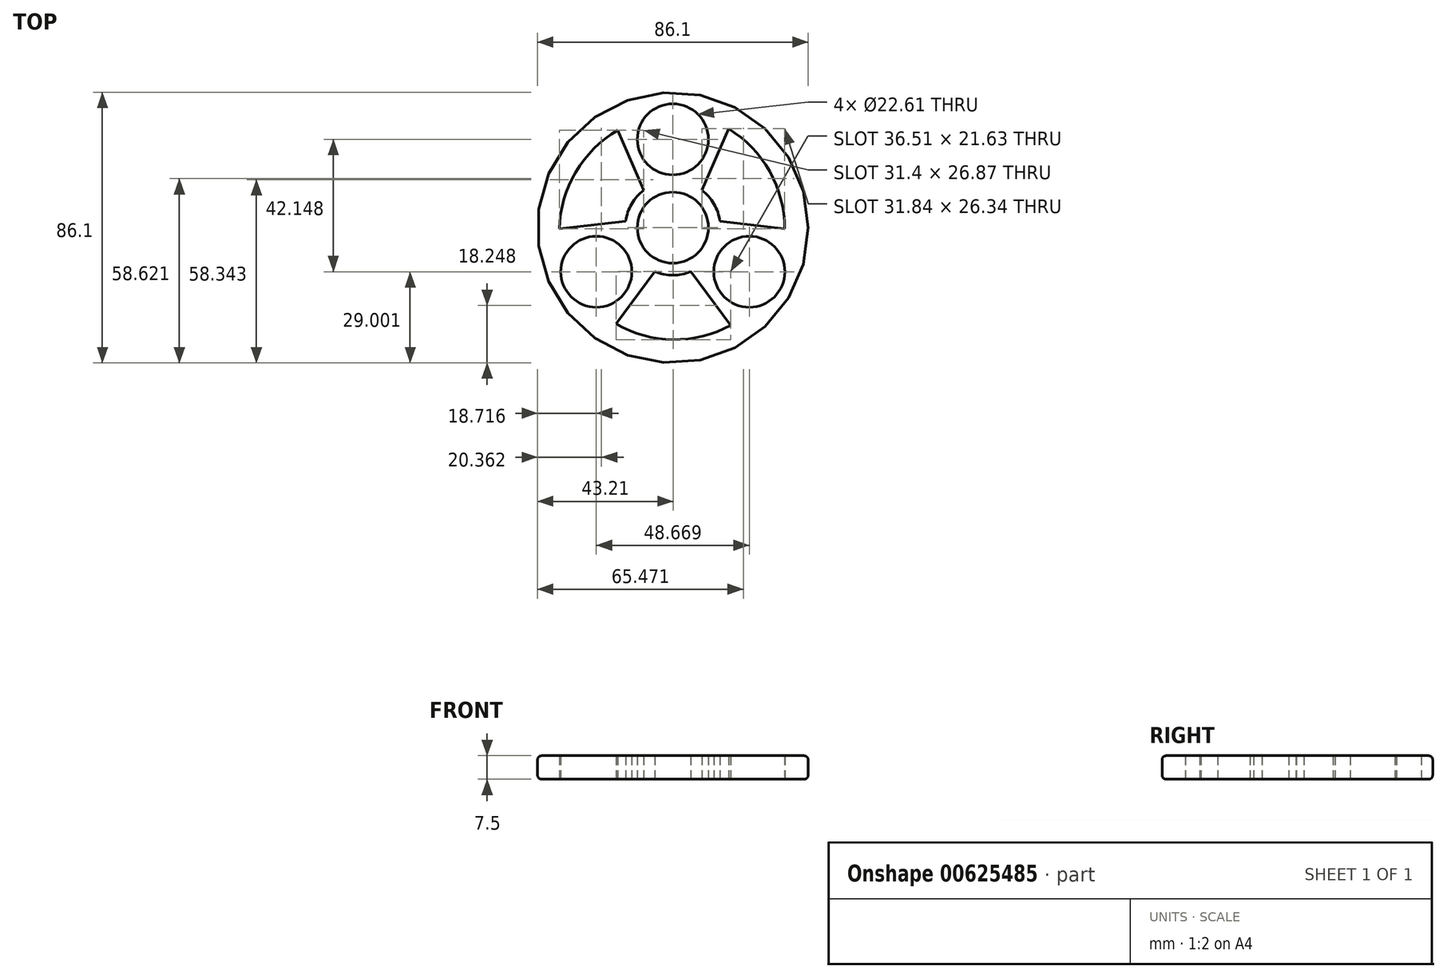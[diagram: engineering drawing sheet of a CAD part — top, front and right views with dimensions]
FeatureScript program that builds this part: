
annotation { "Feature Type Name" : "Feature", "Feature Type Description" : "" }
export const myFeature = defineFeature(function(context is Context, id is Id, definition is map)
    precondition{}
    {
        {
            var Q0;
            Q0=qCreatedBy(makeId("Top.planeOp"),FACE);
            var sketch = newSketch(context, id + "F0", { "sketchPlane" : qUnion([Q0])});
            skCircle(sketch, "E0", {"center": v(0, 0) * mm, "radius": 11.3 * mm});
            skCircle(sketch, "E1", {"center": v(0, 0) * mm, "radius": 15.11 * mm});
            skCircle(sketch, "E2", {"center": v(0, 0) * mm, "radius": 43.05 * mm});
            skLineSegment(sketch, "E3", {"start": v(-9.25, 11.95) * mm, "end": v(-20.47, 37.87) * mm});
            skLineSegment(sketch, "E4", {"start": v(0, 56.55) * mm, "end": v(0, -51.18) * mm});
            skLineSegment(sketch, "E5.MirrorCS", {"start": v(9.25, 11.95) * mm, "end": v(20.47, 37.87) * mm});
            skCircle(sketch, "E6", {"center": v(0, 28.1) * mm, "radius": 11.3 * mm});
            skLineSegment(sketch, "E7.1.0", {"start": v(-14.97, 2.04) * mm, "end": v(-43.04, -1.2) * mm});
            skCircle(sketch, "E7.1.1", {"center": v(-24.33, -14.05) * mm, "radius": 11.3 * mm});
            skLineSegment(sketch, "E7.1.2", {"start": v(-5.72, -13.99) * mm, "end": v(-22.57, -36.67) * mm});
            skLineSegment(sketch, "E7.2.0", {"start": v(5.72, -13.99) * mm, "end": v(22.57, -36.67) * mm});
            skCircle(sketch, "E7.2.1", {"center": v(24.33, -14.05) * mm, "radius": 11.3 * mm});
            skLineSegment(sketch, "E7.2.2", {"start": v(14.97, 2.04) * mm, "end": v(43.04, -1.2) * mm});
            skArc(sketch, "E8", {"start": v(-17.5, 31) * mm, "mid": v(-30.9, 17.72) * mm, "end": v(-36.12, -0.4) * mm});
            skArc(sketch, "E9.1.0", {"start": v(-18.1, -30.65) * mm, "mid": v(0.1, -35.62) * mm, "end": v(18.42, -31.08) * mm});
            skArc(sketch, "E9.2.0", {"start": v(35.59, -0.35) * mm, "mid": v(30.8, 17.9) * mm, "end": v(17.7, 31.49) * mm});
            skSolve(sketch);
        }
        {
            var Q0;
            {var subQ2=sQuery(id+"F0.wireOp",EDGE,"E4");var subQ6=sQuery(id+"F0.wireOp",EDGE,"E0");var subQ9=makeQuery(id+"F0.imprint","INTERSECT",VERTEX,{"disambiguationData":[OD(0.0)],"derivedFrom":[subQ6,subQ2]});Q0=makeQuery(id+"F0.imprint","IMPRINT",FACE,{"disambiguationData":[TD([[makeQuery(id+"F0.imprint","IMPRINT",EDGE,{"disambiguationData":[TD([[subQ9,1.0]])],"derivedFrom":subQ6}),-1.0]])]});}
            var Q1;
            {var subQ4=sQuery(id+"F0.wireOp",EDGE,"E4");var subQ6=sQuery(id+"F0.wireOp",EDGE,"E0");var subQ7=makeQuery(id+"F0.imprint","INTERSECT",VERTEX,{"disambiguationData":[OD(0.0)],"derivedFrom":[subQ6,subQ4]});Q1=makeQuery(id+"F0.imprint","IMPRINT",FACE,{"disambiguationData":[TD([[makeQuery(id+"F0.imprint","IMPRINT",EDGE,{"disambiguationData":[TD([[subQ7,-1.0]])],"derivedFrom":subQ6}),-1.0]])]});}
            var Q2;
            {var subQ0=sQuery(id+"F0.wireOp",EDGE,"E3");var subQ1=sQuery(id+"F0.wireOp",EDGE,"E1");var subQ2=makeQuery(id+"F0.imprint","INTERSECT",VERTEX,{"derivedFrom":[subQ1,subQ0]});Q2=makeQuery(id+"F0.imprint","IMPRINT",FACE,{"disambiguationData":[TD([[makeQuery(id+"F0.imprint","IMPRINT",EDGE,{"disambiguationData":[TD([[subQ2,1.0]])],"derivedFrom":subQ1}),-1.0]])]});}
            var Q3;
            {var subQ1=sQuery(id+"F0.wireOp",EDGE,"E1");var subQ8=sQuery(id+"F0.wireOp",EDGE,"E5.MirrorCS");var subQ10=makeQuery(id+"F0.imprint","INTERSECT",VERTEX,{"derivedFrom":[subQ1,subQ8]});Q3=makeQuery(id+"F0.imprint","IMPRINT",FACE,{"disambiguationData":[TD([[makeQuery(id+"F0.imprint","IMPRINT",EDGE,{"disambiguationData":[TD([[subQ10,-1.0]])],"derivedFrom":subQ1}),-1.0]])]});}
            var Q4;
            {var subQ5=sQuery(id+"F0.wireOp",EDGE,"E9.2.0");Q4=makeQuery(id+"F0.imprint","IMPRINT",FACE,{"disambiguationData":[TD([[makeQuery(id+"F0.imprint","IMPRINT",EDGE,{"derivedFrom":subQ5}),-1.0]])]});}
            var Q5;
            Q5=makeQuery(id+"F0.imprint","IMPRINT",FACE,{"disambiguationData":[TD([[makeQuery(id+"F0.imprint","IMPRINT",EDGE,{"derivedFrom":sQuery(id+"F0.wireOp",EDGE,"E7.2.1")}),-1.0]])]});
            var Q6;
            {var subQ0=sQuery(id+"F0.wireOp",EDGE,"E7.2.0");var subQ1=sQuery(id+"F0.wireOp",EDGE,"E2");var subQ2=makeQuery(id+"F0.imprint","INTERSECT",VERTEX,{"derivedFrom":[subQ1,subQ0]});Q6=makeQuery(id+"F0.imprint","IMPRINT",FACE,{"disambiguationData":[TD([[makeQuery(id+"F0.imprint","IMPRINT",EDGE,{"disambiguationData":[TD([[subQ2,1.0]])],"derivedFrom":subQ1}),1.0]])]});}
            var Q7;
            {var subQ0=sQuery(id+"F0.wireOp",EDGE,"E7.1.2");var subQ1=sQuery(id+"F0.wireOp",EDGE,"E2");var subQ2=makeQuery(id+"F0.imprint","INTERSECT",VERTEX,{"derivedFrom":[subQ1,subQ0]});Q7=makeQuery(id+"F0.imprint","IMPRINT",FACE,{"disambiguationData":[TD([[makeQuery(id+"F0.imprint","IMPRINT",EDGE,{"disambiguationData":[TD([[subQ2,-1.0]])],"derivedFrom":subQ1}),1.0]])]});}
            var Q8;
            Q8=makeQuery(id+"F0.imprint","IMPRINT",FACE,{"disambiguationData":[TD([[makeQuery(id+"F0.imprint","IMPRINT",EDGE,{"derivedFrom":sQuery(id+"F0.wireOp",EDGE,"E7.1.1")}),-1.0]])]});
            var Q9;
            {var subQ5=sQuery(id+"F0.wireOp",EDGE,"E8");Q9=makeQuery(id+"F0.imprint","IMPRINT",FACE,{"disambiguationData":[TD([[makeQuery(id+"F0.imprint","IMPRINT",EDGE,{"derivedFrom":subQ5}),-1.0]])]});}
            extrude(context, id + "F1", {"entities" : qUnion([Q0, Q1, Q2, Q3, Q4, Q5, Q6, Q7, Q8, Q9]), "depth" : 7.5 * mm, "offsetDistance" : 25.4 * mm});
        }
        {
            var Q0;
            Q0=makeQuery(id+"F1.opExtrude","CAP_EDGE",EDGE,{"disambiguationData":[OSD([sQuery(id+"F0.wireOp",EDGE,"E2")])],"isStart":false});
            var Q1;
            Q1=makeQuery(id+"F1.opExtrude","CAP_EDGE",EDGE,{"disambiguationData":[OSD([sQuery(id+"F0.wireOp",EDGE,"E2")])],"isStart":true});
            fillet(context, id + "F2", {"entities" : qUnion([Q0, Q1]), "radius" : 1.52 * mm, "tangentPropagation" : true, "rho" : 0.5, "crossSection" : FilletCrossSection.CONIC, "allowEdgeOverflow" : false});
        }
    });
